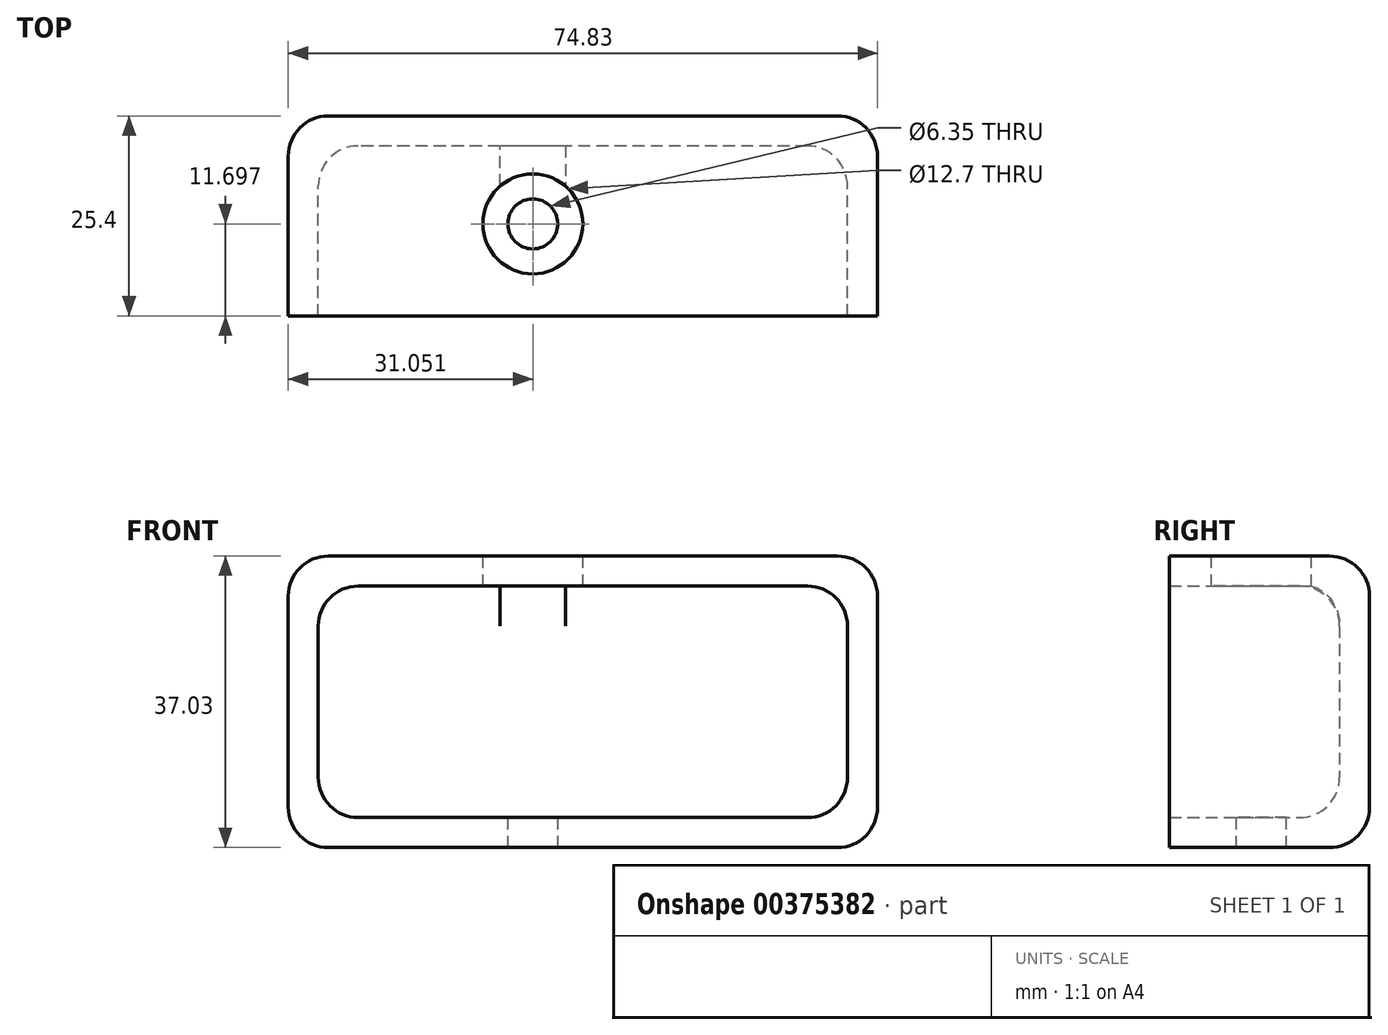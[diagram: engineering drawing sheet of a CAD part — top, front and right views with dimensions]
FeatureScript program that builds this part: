
annotation { "Feature Type Name" : "Feature", "Feature Type Description" : "" }
export const myFeature = defineFeature(function(context is Context, id is Id, definition is map)
    precondition{}
    {
        {
            var Q0;
            Q0=qCreatedBy(makeId("Front.planeOp"),FACE);
            var sketch = newSketch(context, id + "F0", { "sketchPlane" : qUnion([Q0])});
            skLineSegment(sketch, "E0.bottom", {"start": v(0, 0) * mm, "end": v(-74.83, 0) * mm});
            skLineSegment(sketch, "E0.top", {"start": v(0, -37.03) * mm, "end": v(-74.83, -37.03) * mm});
            skLineSegment(sketch, "E0.left", {"start": v(0, 0) * mm, "end": v(0, -37.03) * mm});
            skLineSegment(sketch, "E0.right", {"start": v(-74.83, 0) * mm, "end": v(-74.83, -37.03) * mm});
            skSolve(sketch);
        }
        {
            var Q0;
            Q0 = qSketchRegion(id + "F0", true);
            extrude(context, id + "F1", {"entities" : qUnion([Q0]), "depth" : 25.4 * mm});
        }
        {
            var Q0;
            Q0=makeQuery(id+"F1.opExtrude","CAP_FACE",FACE,{"disambiguationData":[OSD([sQuery(id+"F0.wireOp",EDGE,"E0.bottom"),sQuery(id+"F0.wireOp",EDGE,"E0.top"),sQuery(id+"F0.wireOp",EDGE,"E0.left"),sQuery(id+"F0.wireOp",EDGE,"E0.right")])],"isStart":false});
            shell(context, id + "F2", {"entities" : qUnion([Q0]), "thickness" : 3.8 * mm});
        }
        {
            var Q0;
            Q0=makeQuery(id+"F1.opExtrude","SWEPT_FACE",FACE,{"disambiguationData":[OSD([sQuery(id+"F0.wireOp",EDGE,"E0.bottom")])]});
            var sketch = newSketch(context, id + "F3", { "sketchPlane" : qUnion([Q0])});
            skCircle(sketch, "E1", {"center": v(-43.78, -13.7) * mm, "radius": 4.28 * mm});
            skSolve(sketch);
        }
        {
            var Q0;
            Q0=sQuery(id+"F3.wireOp",VERTEX,"E1.center");
            var Q1;
            Q1=makeQuery(id+"F1.opExtrude","SWEPT_BODY",BODY,{"disambiguationData":[OSD([sQuery(id+"F0.wireOp",EDGE,"E0.bottom"),sQuery(id+"F0.wireOp",EDGE,"E0.top"),sQuery(id+"F0.wireOp",EDGE,"E0.left"),sQuery(id+"F0.wireOp",EDGE,"E0.right")])]});
            hole(context, id + "F4", {"style" : HoleStyle.C_BORE, "endStyle" : HoleEndStyle.THROUGH, "holeDiameter" : 6.35 * mm, "cBoreDiameter" : 12.7 * mm, "cBoreDepth" : 6.35 * mm, "isTappedThrough" : true, "tappedDepth" : 12.7 * mm, "tapClearance" : 3, "startFromSketch" : true, "locations" : qUnion([Q0]), "scope" : qUnion([Q1])});
        }
        {
            var Q0;
            Q0=makeQuery(id+"F1.opExtrude","CAP_EDGE",EDGE,{"disambiguationData":[OSD([sQuery(id+"F0.wireOp",EDGE,"E0.bottom")])],"isStart":true});
            fillet(context, id + "F5", {"entities" : qUnion([Q0]), "radius" : 5.08 * mm, "tangentPropagation" : true, "allowEdgeOverflow" : false});
        }
        {
            var Q0;
            Q0=makeQuery(id+"F1.opExtrude","CAP_EDGE",EDGE,{"disambiguationData":[OSD([sQuery(id+"F0.wireOp",EDGE,"E0.left")])],"isStart":true});
            var Q1;
            Q1=makeQuery(id+"F1.opExtrude","SWEPT_EDGE",EDGE,{"disambiguationData":[OSD([sQuery(id+"F0.wireOp",EDGE,"E0.top"),sQuery(id+"F0.wireOp",EDGE,"E0.left")])]});
            fillet(context, id + "F6", {"entities" : qUnion([Q0, Q1]), "radius" : 5.08 * mm, "tangentPropagation" : true, "allowEdgeOverflow" : false});
        }
        {
            var Q0;
            Q0=makeQuery(id+"F1.opExtrude","SWEPT_EDGE",EDGE,{"disambiguationData":[OSD([sQuery(id+"F0.wireOp",EDGE,"E0.bottom"),sQuery(id+"F0.wireOp",EDGE,"E0.right")])]});
            fillet(context, id + "F7", {"entities" : qUnion([Q0]), "radius" : 5.08 * mm, "tangentPropagation" : true, "allowEdgeOverflow" : false});
        }
        {
            var Q0;
            Q0=makeQuery(id+"F2.opShell","OFFSET_EDGE",EDGE,{"disambiguationData":[OSD([sQuery(id+"F0.wireOp",EDGE,"E0.top"),sQuery(id+"F0.wireOp",EDGE,"E0.right")])]});
            fillet(context, id + "F8", {"entities" : qUnion([Q0]), "radius" : 5.08 * mm, "tangentPropagation" : true, "allowEdgeOverflow" : false});
        }
        {
            var Q0;
            Q0=makeQuery(id+"F1.opExtrude","CAP_EDGE",EDGE,{"disambiguationData":[OSD([sQuery(id+"F0.wireOp",EDGE,"E0.top")])],"isStart":true});
            fillet(context, id + "F9", {"entities" : qUnion([Q0]), "radius" : 5.08 * mm, "tangentPropagation" : true, "allowEdgeOverflow" : false});
        }
        {
            var Q0;
            Q0=makeQuery(id+"F2.opShell","OFFSET_EDGE",EDGE,{"disambiguationData":[OSD([sQuery(id+"F0.wireOp",EDGE,"E0.bottom"),sQuery(id+"F0.wireOp",EDGE,"E0.right")])]});
            fillet(context, id + "F10", {"entities" : qUnion([Q0]), "radius" : 5.08 * mm, "tangentPropagation" : true, "allowEdgeOverflow" : false});
        }
        {
            var Q0;
            {var subQ0=sQuery(id+"F0.wireOp",EDGE,"E0.bottom");Q0=makeQuery(id+"F2.opShell","OFFSET_EDGE",EDGE,{"disambiguationData":[OSD([subQ0]),TDD([makeQuery(id+"F1.opExtrude","CAP_EDGE",EDGE,{"disambiguationData":[OSD([subQ0])],"isStart":true})])]});}
            fillet(context, id + "F11", {"entities" : qUnion([Q0]), "radius" : 5.08 * mm, "tangentPropagation" : true, "allowEdgeOverflow" : false});
        }
        {
            var Q0;
            Q0=makeQuery(id+"F2.opShell","OFFSET_EDGE",EDGE,{"disambiguationData":[OSD([sQuery(id+"F0.wireOp",EDGE,"E0.bottom"),sQuery(id+"F0.wireOp",EDGE,"E0.left")])]});
            fillet(context, id + "F12", {"entities" : qUnion([Q0]), "radius" : 5.08 * mm, "tangentPropagation" : true, "allowEdgeOverflow" : false});
        }
    });
